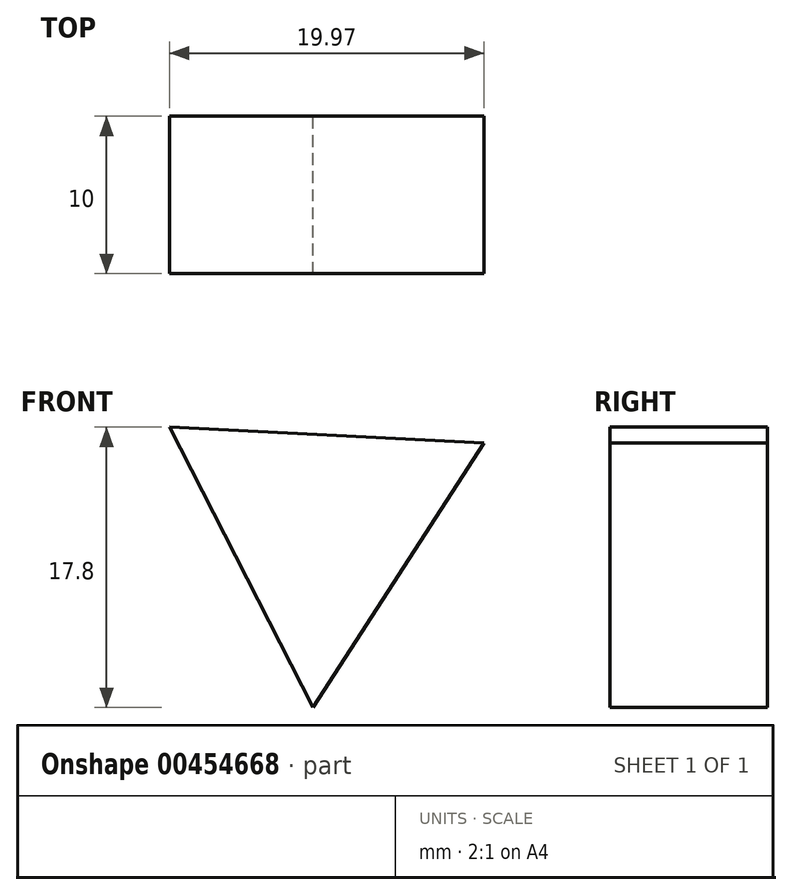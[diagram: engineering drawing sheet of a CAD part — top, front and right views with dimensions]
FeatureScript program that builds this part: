
annotation { "Feature Type Name" : "Feature", "Feature Type Description" : "" }
export const myFeature = defineFeature(function(context is Context, id is Id, definition is map)
    precondition{}
    {
        {
            var Q0;
            Q0=qCreatedBy(makeId("Front.planeOp"),FACE);
            var sketch = newSketch(context, id + "F0", { "sketchPlane" : qUnion([Q0])});
            skCircle(sketch, "E0.cCircle", {"center": v(0, 0) * mm, "radius": 5.77 * mm, "construction": true});
            skLineSegment(sketch, "E0.0", {"start": v(-9.7, 6.27) * mm, "end": v(10.28, 5.26) * mm});
            skLineSegment(sketch, "E0.1", {"start": v(10.28, 5.26) * mm, "end": v(-0.59, -11.53) * mm});
            skLineSegment(sketch, "E0.2", {"start": v(-0.59, -11.53) * mm, "end": v(-9.7, 6.27) * mm});
            skPoint(sketch, "E0.0.midPoint", {"position": v(0.3, 5.77) * mm});
            skSolve(sketch);
        }
        {
            var Q0;
            Q0 = qSketchRegion(id + "F0", true);
            extrude(context, id + "F1", {"entities" : qUnion([Q0]), "depth" : 10 * mm});
        }
    });
